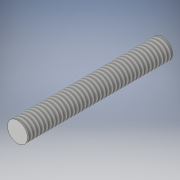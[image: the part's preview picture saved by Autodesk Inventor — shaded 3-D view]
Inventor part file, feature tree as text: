
AUTODESK INVENTOR PART (.ipt)
format: ipt  version: 2017 (Build 210142000, 142)  size: 102,400 bytes
history: native  units: in
note: dims shown in document units (in); Inventor stores cm internally (conversion verified against a paired STEP export)
features: extrude x2, sketch x2, thread x1
ambient origin geometry x8: Origin, YZ Plane, XZ Plane, XY Plane, X Axis, Y Axis, Z Axis, Center Point
bodies: Solid1 (feature_tree)
feature tree (5):
  extrude  "Extrusion1"  Depth=3.0in TaperAngle=0.0deg
  thread  "Thread1"  [1 undecoded]
  extrude  "Extrusion2"  [1 undecoded]
  sketch  "Sketch1"  dims[d0=0.164in d1=3.0in d2=0.0in d3=1.0in d4=0.0in]
  sketch  "Sketch2"  dims[d5=1.1811in d6=0.0in]
note: 2 required parameter values undecoded (feature->parameter linkage not recoverable at this tier; creation-order binding heuristic only, values carry confidence <= 0.55)
